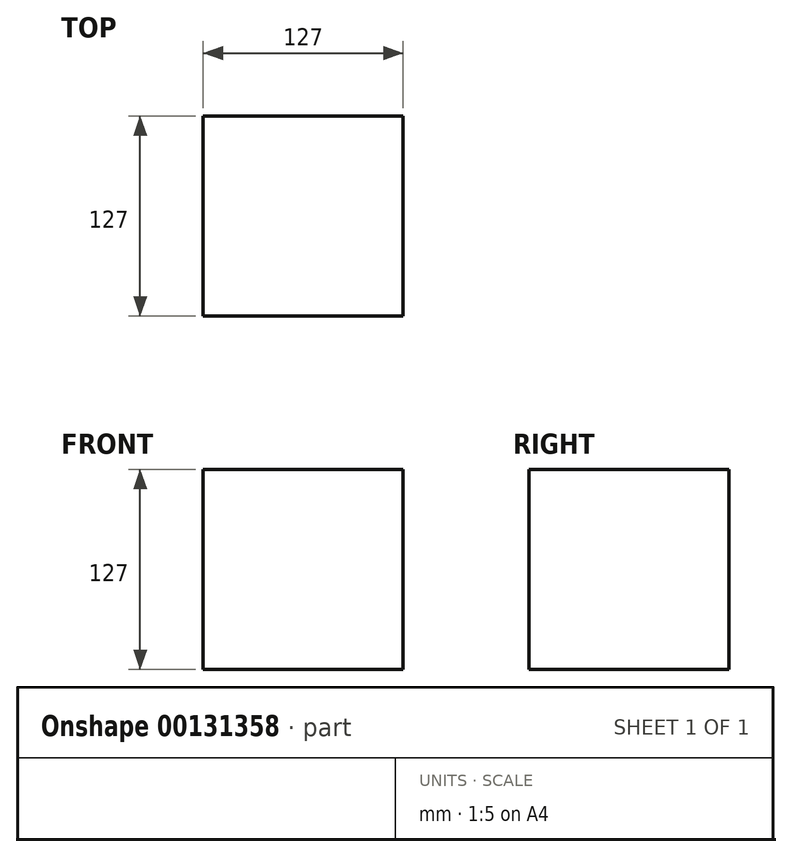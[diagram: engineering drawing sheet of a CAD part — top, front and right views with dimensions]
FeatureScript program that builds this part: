
annotation { "Feature Type Name" : "Feature", "Feature Type Description" : "" }
export const myFeature = defineFeature(function(context is Context, id is Id, definition is map)
    precondition{}
    {
        {
            var Q0;
            Q0=qCreatedBy(makeId("Front.planeOp"),FACE);
            var sketch = newSketch(context, id + "F0", { "sketchPlane" : qUnion([Q0])});
            skLineSegment(sketch, "E0.bottom", {"start": v(-63.5, -63.5) * mm, "end": v(63.5, -63.5) * mm});
            skLineSegment(sketch, "E0.top", {"start": v(-63.5, 63.5) * mm, "end": v(63.5, 63.5) * mm});
            skLineSegment(sketch, "E0.left", {"start": v(-63.5, -63.5) * mm, "end": v(-63.5, 63.5) * mm});
            skLineSegment(sketch, "E0.right", {"start": v(63.5, -63.5) * mm, "end": v(63.5, 63.5) * mm});
            skPoint(sketch, "E0.middle", {"position": v(0, 0) * mm});
            skSolve(sketch);
        }
        {
            var Q0;
            Q0=makeQuery(id+"F0.imprint","IMPRINT",FACE,{"disambiguationData":[TD([[makeQuery(id+"F0.imprint","IMPRINT",EDGE,{"derivedFrom":sQuery(id+"F0.wireOp",EDGE,"E0.bottom")}),1.0]])]});
            extrude(context, id + "F1", {"entities" : qUnion([Q0]), "depth" : 127 * mm});
        }
    });
